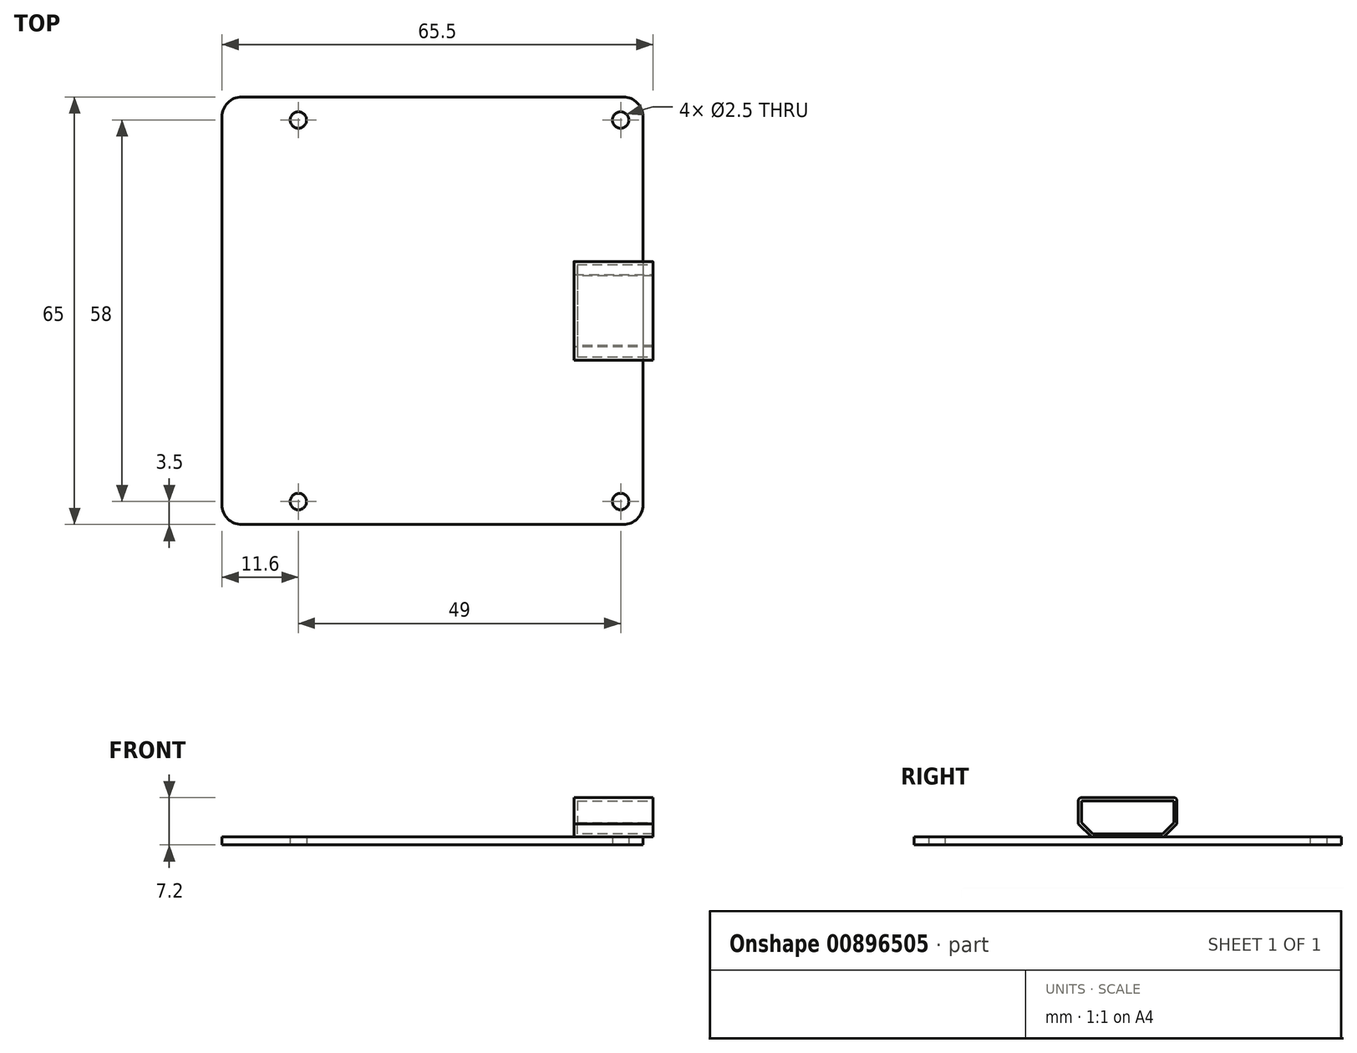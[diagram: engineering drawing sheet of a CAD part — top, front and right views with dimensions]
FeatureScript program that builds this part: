
annotation { "Feature Type Name" : "Feature", "Feature Type Description" : "" }
export const myFeature = defineFeature(function(context is Context, id is Id, definition is map)
    precondition{}
    {
        {
            var Q0;
            Q0=qCreatedBy(makeId("Top.planeOp"),FACE);
            var sketch = newSketch(context, id + "F0", { "sketchPlane" : qUnion([Q0])});
            skLineSegment(sketch, "E0.bottom", {"start": v(32, 32.5) * mm, "end": v(-32, 32.5) * mm});
            skLineSegment(sketch, "E0.top", {"start": v(32, -32.5) * mm, "end": v(-32, -32.5) * mm});
            skLineSegment(sketch, "E0.left", {"start": v(32, 32.5) * mm, "end": v(32, -32.5) * mm});
            skLineSegment(sketch, "E0.right", {"start": v(-32, 32.5) * mm, "end": v(-32, -32.5) * mm});
            skPoint(sketch, "E0.middle", {"position": v(0, 0) * mm});
            skCircle(sketch, "E1", {"center": v(28.6, 29) * mm, "radius": 1.25 * mm});
            skCircle(sketch, "E2", {"center": v(28.6, -29) * mm, "radius": 1.25 * mm});
            skCircle(sketch, "E3", {"center": v(-20.4, -29) * mm, "radius": 1.25 * mm});
            skCircle(sketch, "E4", {"center": v(-20.4, 29) * mm, "radius": 1.25 * mm});
            skLineSegment(sketch, "E5", {"start": v(28.6, 29) * mm, "end": v(-20.4, 29) * mm, "construction": true});
            skLineSegment(sketch, "E6", {"start": v(28.6, 29) * mm, "end": v(28.6, -29) * mm, "construction": true});
            skSolve(sketch);
        }
        {
            var Q0;
            Q0 = qSketchRegion(id + "F0", true);
            extrude(context, id + "F1", {"entities" : qUnion([Q0]), "depth" : 1.2 * mm, "offsetDistance" : 25 * mm});
        }
        {
            var Q0;
            Q0=makeQuery(id+"F1.opExtrude","SWEPT_EDGE",EDGE,{"disambiguationData":[OSD([sQuery(id+"F0.wireOp",EDGE,"E0.bottom"),sQuery(id+"F0.wireOp",EDGE,"E0.right")])]});
            var Q1;
            Q1=makeQuery(id+"F1.opExtrude","SWEPT_EDGE",EDGE,{"disambiguationData":[OSD([sQuery(id+"F0.wireOp",EDGE,"E0.bottom"),sQuery(id+"F0.wireOp",EDGE,"E0.left")])]});
            var Q2;
            Q2=makeQuery(id+"F1.opExtrude","SWEPT_EDGE",EDGE,{"disambiguationData":[OSD([sQuery(id+"F0.wireOp",EDGE,"E0.top"),sQuery(id+"F0.wireOp",EDGE,"E0.left")])]});
            var Q3;
            Q3=makeQuery(id+"F1.opExtrude","SWEPT_EDGE",EDGE,{"disambiguationData":[OSD([sQuery(id+"F0.wireOp",EDGE,"E0.top"),sQuery(id+"F0.wireOp",EDGE,"E0.right")])]});
            fillet(context, id + "F2", {"entities" : qUnion([Q0, Q1, Q2, Q3]), "tangentPropagation" : true, "radius" : 3 * mm, "defaultsChanged" : true, "vertexSettings" : [], "allowEdgeOverflow" : false});
        }
        {
            var Q0;
            Q0=makeQuery(id+"F1.opExtrude","CAP_FACE",FACE,{"disambiguationData":[OSD([sQuery(id+"F0.wireOp",EDGE,"E0.bottom"),sQuery(id+"F0.wireOp",EDGE,"E0.top"),sQuery(id+"F0.wireOp",EDGE,"E0.left"),sQuery(id+"F0.wireOp",EDGE,"E0.right"),sQuery(id+"F0.wireOp",EDGE,"E1"),sQuery(id+"F0.wireOp",EDGE,"E2"),sQuery(id+"F0.wireOp",EDGE,"E3"),sQuery(id+"F0.wireOp",EDGE,"E4")])],"isStart":false});
            var sketch = newSketch(context, id + "F3", { "sketchPlane" : qUnion([Q0])});
            skLineSegment(sketch, "E7.bottom", {"start": v(33.5, 7.5) * mm, "end": v(21.5, 7.5) * mm});
            skLineSegment(sketch, "E7.top", {"start": v(33.5, -7.5) * mm, "end": v(21.5, -7.5) * mm});
            skLineSegment(sketch, "E7.left", {"start": v(33.5, 7.5) * mm, "end": v(33.5, -7.5) * mm});
            skLineSegment(sketch, "E7.right", {"start": v(21.5, 7.5) * mm, "end": v(21.5, -7.5) * mm});
            skPoint(sketch, "E7.middle", {"position": v(27.5, 0) * mm});
            skSolve(sketch);
        }
        {
            var Q0;
            Q0 = qSketchRegion(id + "F3", true);
            extrude(context, id + "F4", {"entities" : qUnion([Q0]), "depth" : 6 * mm, "offsetDistance" : 25 * mm});
        }
        {
            var Q0;
            Q0=makeQuery(id+"F4.opExtrude","CAP_EDGE",EDGE,{"disambiguationData":[OSD([sQuery(id+"F3.wireOp",EDGE,"E7.top")])],"isStart":true});
            var Q1;
            Q1=makeQuery(id+"F4.opExtrude","CAP_EDGE",EDGE,{"disambiguationData":[OSD([sQuery(id+"F3.wireOp",EDGE,"E7.bottom")])],"isStart":true});
            chamfer(context, id + "F5", {"entities" : qUnion([Q0, Q1]), "width" : 2 * mm, "tangentPropagation" : true});
        }
        {
            var Q0;
            Q0=makeQuery(id+"F4.opExtrude","CAP_EDGE",EDGE,{"disambiguationData":[OSD([sQuery(id+"F3.wireOp",EDGE,"E7.top")])],"isStart":false});
            var Q1;
            Q1=makeQuery(id+"F4.opExtrude","CAP_EDGE",EDGE,{"disambiguationData":[OSD([sQuery(id+"F3.wireOp",EDGE,"E7.bottom")])],"isStart":false});
            fillet(context, id + "F6", {"entities" : qUnion([Q0, Q1]), "tangentPropagation" : true, "radius" : 0.5 * mm, "defaultsChanged" : true, "vertexSettings" : [], "allowEdgeOverflow" : false});
        }
        {
            var Q0;
            Q0=makeQuery(id+"F4.opExtrude","SWEPT_FACE",FACE,{"disambiguationData":[OSD([sQuery(id+"F3.wireOp",EDGE,"E7.left")])]});
            shell(context, id + "F7", {"entities" : qUnion([Q0]), "thickness" : 0.5 * mm});
        }
    });
